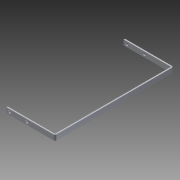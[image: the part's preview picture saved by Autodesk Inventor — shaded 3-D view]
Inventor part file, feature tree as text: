
AUTODESK INVENTOR PART (.ipt)
format: ipt  version: 2013 (Build 170138000, 138)  size: 205,312 bytes
history: native  units: in
note: dims shown in document units (in); Inventor stores cm internally (conversion verified against a paired STEP export)
features: sheet_metal_op x7, sketch x7, other x6, extrude x2, reference x2
ambient origin geometry x8: Origin, YZ Plane, XZ Plane, XY Plane, X Axis, Y Axis, Z Axis, Center Point
feature tree (24):
  sheet_metal_op  "Face2"
  sheet_metal_op  "Flange4"
  sheet_metal_op  "Flange5"
  extrude  "Extrusion3"  Depth=0.5in
  extrude  "Extrusion4"  Depth=0.125in
  sketch  "Sketch1"  dims[d1=4.494in d2=0.5in]
  other  "Plate5"
  sketch  "Sketch6"  dims[d42=0.125in]
  other  "Plate6"
  sheet_metal_op  "Bend4"
  sheet_metal_op  "Corner4"
  sketch  "Sketch7"  dims[d43=0.125in]
  other  "Plate7"
  sheet_metal_op  "Bend5"
  sheet_metal_op  "Corner5"
  sketch  "Sketch12"  dims[d44=0.0625in]
  sketch  "Sketch13"  dims[d45=0.25in]
  reference  "Reference3"
  reference  "Reference4"
  sketch  "Sketch14"  dims[d46=0.125in d47=11.218in d48=90.0deg d49=0.05in d50=0.5in d51=0.125in d52=0.125in d53=0.125in d54=0.0625in d55=0.25in d56=0.125in d57=4.669in d58=90.0deg d59=0.05in d60=0.5in d61=0.125in d62=0.125in d66=0.26in d67=0.295in d70=1.9482in d71=999.0in d72=0.0in d73=0.125in d74=0.0in d75=20.0in d76=0.0in d0=4.576in d3=0.0625in d4=0.0625in d6=0.0312in d7=4.576in d9=0.0312in d10=0.0625in d11=0.125in d12=0.0in d13=0.0312in d14=0.125in d15=0.0in]
  other  "Cut1"
  other  "Definition1"
  sketch  "Sketch2"  dims[d5=0.295in d8=0.125in]
  other  "Cut2"
